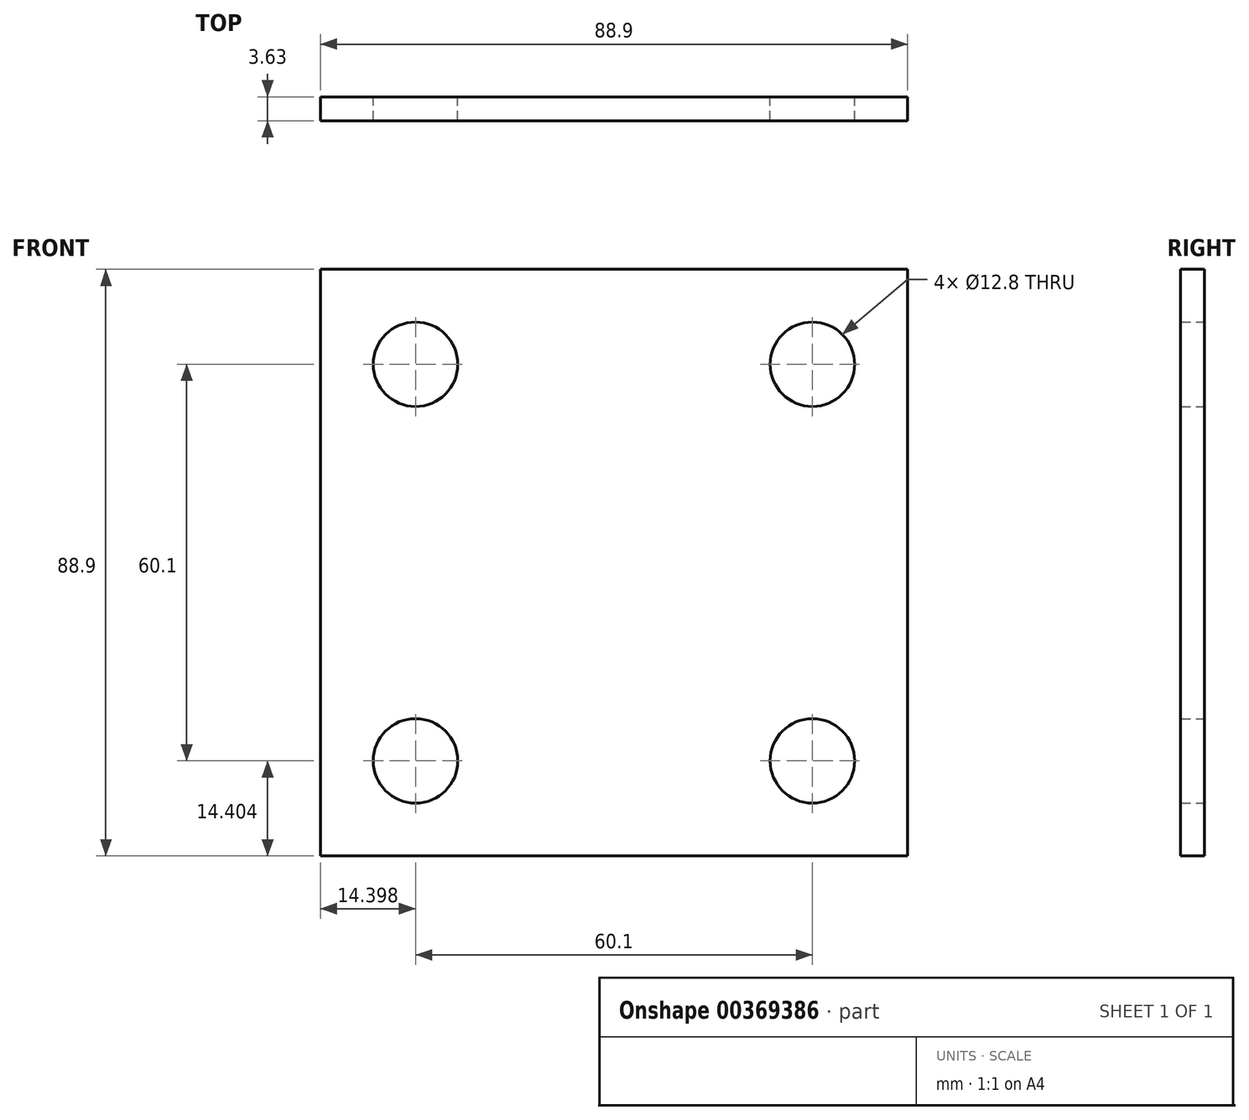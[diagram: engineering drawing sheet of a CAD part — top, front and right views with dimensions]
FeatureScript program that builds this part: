
annotation { "Feature Type Name" : "Feature", "Feature Type Description" : "" }
export const myFeature = defineFeature(function(context is Context, id is Id, definition is map)
    precondition{}
    {
        {
            var Q0;
            Q0=qCreatedBy(makeId("Front.planeOp"),FACE);
            var sketch = newSketch(context, id + "F0", { "sketchPlane" : qUnion([Q0])});
            skLineSegment(sketch, "E0", {"start": v(-51.14, 49.44) * mm, "end": v(-51.14, -39.46) * mm});
            skLineSegment(sketch, "E1", {"start": v(-51.14, -39.46) * mm, "end": v(37.76, -39.46) * mm});
            skLineSegment(sketch, "E2", {"start": v(37.76, -39.46) * mm, "end": v(37.76, 49.44) * mm});
            skLineSegment(sketch, "E3", {"start": v(37.76, 49.44) * mm, "end": v(-51.14, 49.44) * mm});
            skSolve(sketch);
        }
        {
            var Q0;
            Q0 = qSketchRegion(id + "F0", true);
            extrude(context, id + "F1", {"entities" : qUnion([Q0]), "depth" : 3.63 * mm});
        }
        {
            var Q0;
            Q0=makeQuery(id+"F0.imprint","IMPRINT",FACE,{"disambiguationData":[TD([[makeQuery(id+"F0.imprint","IMPRINT",EDGE,{"derivedFrom":sQuery(id+"F0.wireOp",EDGE,"E0")}),1.0]])]});
            var sketch = newSketch(context, id + "F2", { "sketchPlane" : qUnion([Q0])});
            skCircle(sketch, "E4", {"center": v(23.36, 35.04) * mm, "radius": 6.4 * mm});
            skCircle(sketch, "E5", {"center": v(-36.74, 35.04) * mm, "radius": 6.4 * mm});
            skCircle(sketch, "E6", {"center": v(23.36, -25.06) * mm, "radius": 6.4 * mm});
            skCircle(sketch, "E7", {"center": v(-36.74, -25.06) * mm, "radius": 6.4 * mm});
            skSolve(sketch);
        }
        {
            var Q0;
            Q0=makeQuery(id+"F2.imprint","IMPRINT",FACE,{"disambiguationData":[TD([[makeQuery(id+"F2.imprint","IMPRINT",EDGE,{"derivedFrom":sQuery(id+"F2.wireOp",EDGE,"E4")}),1.0]])]});
            var Q1;
            Q1=makeQuery(id+"F2.imprint","IMPRINT",FACE,{"disambiguationData":[TD([[makeQuery(id+"F2.imprint","IMPRINT",EDGE,{"derivedFrom":sQuery(id+"F2.wireOp",EDGE,"E6")}),1.0]])]});
            var Q2;
            Q2=makeQuery(id+"F2.imprint","IMPRINT",FACE,{"disambiguationData":[TD([[makeQuery(id+"F2.imprint","IMPRINT",EDGE,{"derivedFrom":sQuery(id+"F2.wireOp",EDGE,"E7")}),1.0]])]});
            var Q3;
            Q3=makeQuery(id+"F2.imprint","IMPRINT",FACE,{"disambiguationData":[TD([[makeQuery(id+"F2.imprint","IMPRINT",EDGE,{"derivedFrom":sQuery(id+"F2.wireOp",EDGE,"E5")}),1.0]])]});
            extrude(context, id + "F3", {"entities" : qUnion([Q0, Q1, Q2, Q3]), "operationType" : NewBodyOperationType.REMOVE, "depth" : 46.5 * mm});
        }
    });
